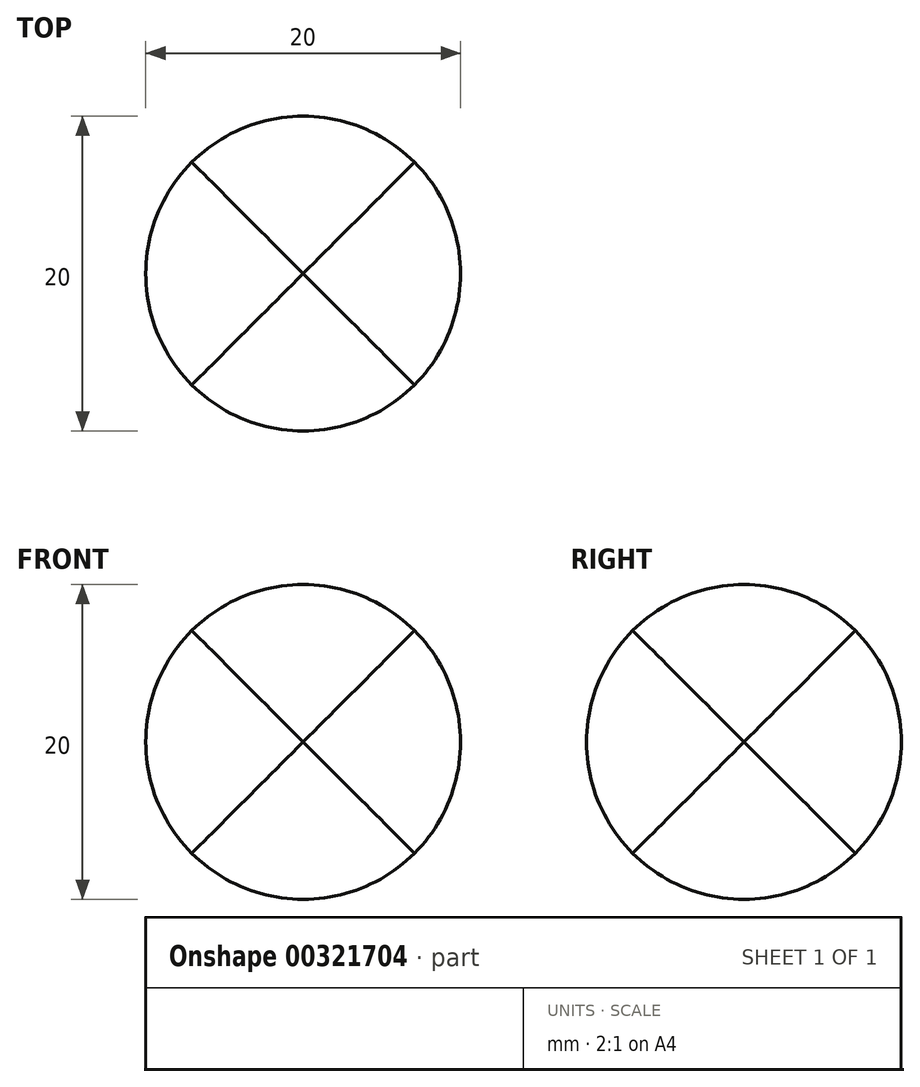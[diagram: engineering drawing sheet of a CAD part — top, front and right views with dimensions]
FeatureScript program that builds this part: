
annotation { "Feature Type Name" : "Feature", "Feature Type Description" : "" }
export const myFeature = defineFeature(function(context is Context, id is Id, definition is map)
    precondition{}
    {
        {
            var Q0;
            Q0=qCreatedBy(makeId("Front.planeOp"),FACE);
            var sketch = newSketch(context, id + "F0", { "sketchPlane" : qUnion([Q0])});
            skCircle(sketch, "E0", {"center": v(0, 0) * mm, "radius": 10 * mm});
            skSolve(sketch);
        }
        {
            var Q0;
            Q0=makeQuery(id+"F0.imprint","IMPRINT",FACE,{"disambiguationData":[TD([[makeQuery(id+"F0.imprint","IMPRINT",EDGE,{"derivedFrom":sQuery(id+"F0.wireOp",EDGE,"E0")}),1.0]])]});
            extrude(context, id + "F1", {"entities" : qUnion([Q0]), "endBound" : BoundingType.SYMMETRIC, "depth" : 76.2 * mm});
        }
        {
            var Q0;
            Q0=qCreatedBy(makeId("Front.planeOp"),FACE);
            var Q1;
            Q1=qCreatedBy(makeId("Right.planeOp"),FACE);
            cPlane(context, id + "F2", {"entities" : qUnion([Q0, Q1]), "cplaneType" : CPlaneType.MID_PLANE, "offset" : 25.4 * mm, "width" : 152.4 * mm, "height" : 152.4 * mm});
        }
        {
            var Q0;
            Q0=qCreatedBy(id+"F2.planeOp",FACE);
            var sketch = newSketch(context, id + "F3", { "sketchPlane" : qUnion([Q0])});
            skLineSegment(sketch, "E1", {"start": v(0, 0) * mm, "end": v(-28.28, 20) * mm});
            skSolve(sketch);
        }
        {
            var Q0;
            Q0=makeQuery(id+"F1.opExtrude","SWEPT_BODY",BODY,{"disambiguationData":[OSD([sQuery(id+"F0.wireOp",EDGE,"E0")])]});
            var Q1;
            Q1=sQuery(id+"F3.wireOp",EDGE,"E1");
            circularPattern(context, id + "F4", {"entities" : qUnion([Q0]), "axis" : qUnion([Q1]), "angle" : 360 * degree, "instanceCount" : 3, "equalSpace" : true});
        }
        {
            var Q0;
            Q0=makeQuery(id+"F4.opPattern","COPY",BODY,{"derivedFrom":makeQuery(id+"F1.opExtrude","SWEPT_BODY",BODY,{"disambiguationData":[OSD([sQuery(id+"F0.wireOp",EDGE,"E0")])]}),"instanceName":"2"});
            var Q1;
            Q1=makeQuery(id+"F4.opPattern","COPY",BODY,{"derivedFrom":makeQuery(id+"F1.opExtrude","SWEPT_BODY",BODY,{"disambiguationData":[OSD([sQuery(id+"F0.wireOp",EDGE,"E0")])]}),"instanceName":"1"});
            var Q2;
            Q2=makeQuery(id+"F1.opExtrude","SWEPT_BODY",BODY,{"disambiguationData":[OSD([sQuery(id+"F0.wireOp",EDGE,"E0")])]});
            booleanBodies(context, id + "F5", {"operationType" : BooleanOperationType.INTERSECTION, "tools" : qUnion([Q0, Q1, Q2])});
        }
    });
